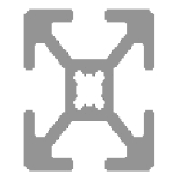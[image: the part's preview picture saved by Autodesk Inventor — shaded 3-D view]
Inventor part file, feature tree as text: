
AUTODESK INVENTOR PART (.ipt)
format: ipt  version: 2013 SP2 (Build 170200200, 200)  size: 232,960 bytes
history: native  units: in
note: dims shown in document units (in); Inventor stores cm internally (conversion verified against a paired STEP export)
features: other x5, sketch x3, plane x1
ambient origin geometry x8: Origin, YZ Plane, XZ Plane, XY Plane, X Axis, Y Axis, Z Axis, Center Point
bodies: Solid1 (feature_tree), Body (feature_tree)
feature tree (9):
  other  "Driven Length"
  other  "Frame Generator"
  other  "Blocks"
  other  "Start Plane"
  other  "End Plane"
  sketch  "Sketch"  dims[d4=0.13in d5=0.0in d6=90.0deg d7=16.5354in]
  sketch  "Sketch2"  dims[d2=0.7874in]
  plane  "Work Plane3"
  sketch  "Sketch3"  dims[d3=17.3228in]
